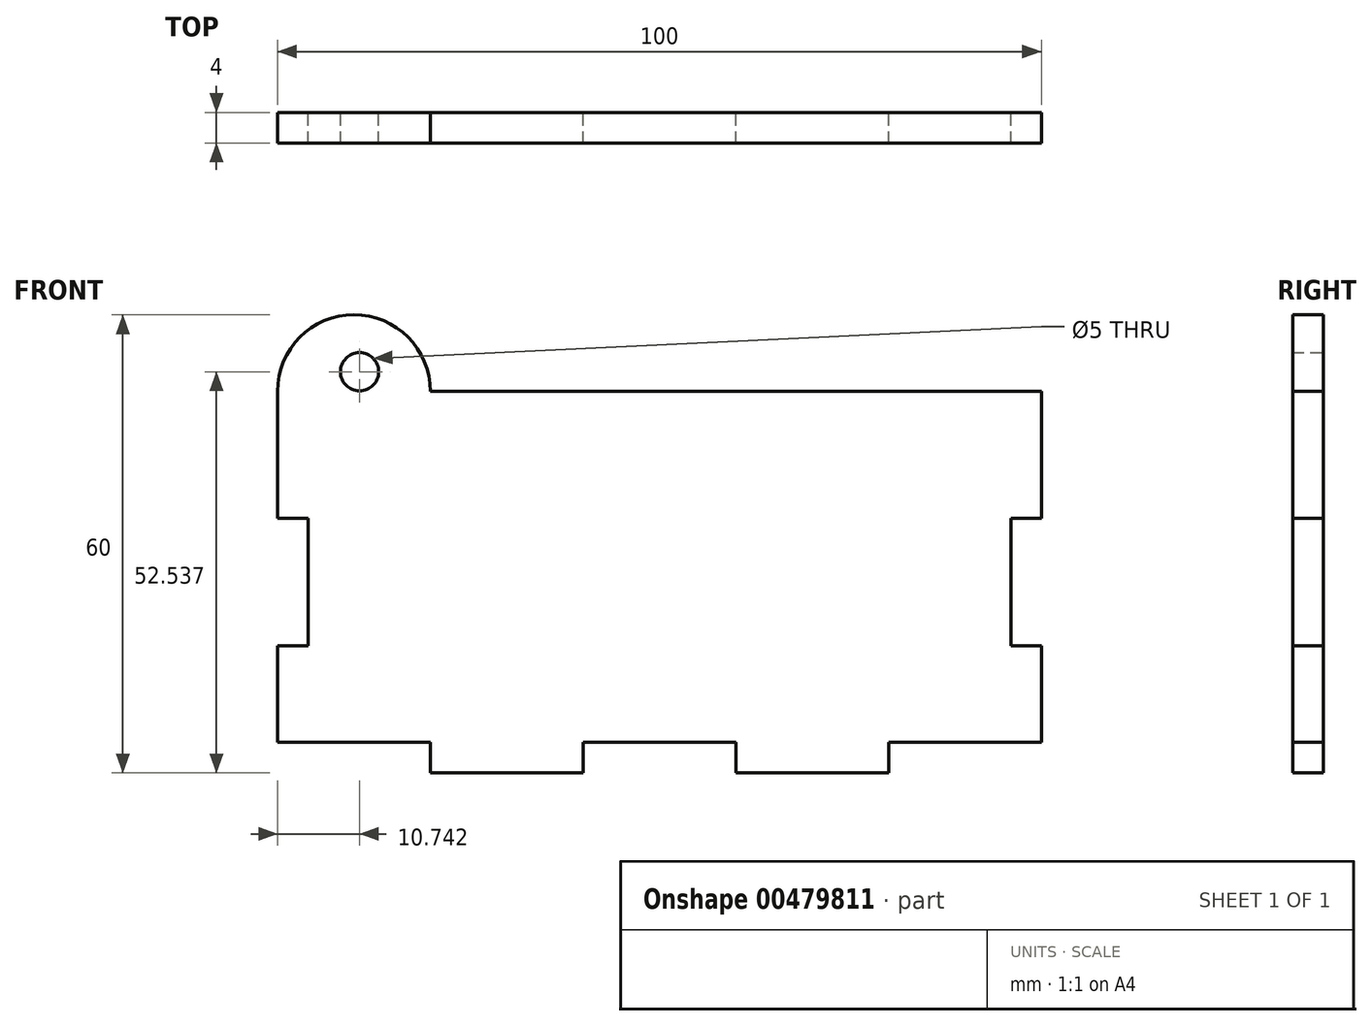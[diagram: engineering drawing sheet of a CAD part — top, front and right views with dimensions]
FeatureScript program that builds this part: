
annotation { "Feature Type Name" : "Feature", "Feature Type Description" : "" }
export const myFeature = defineFeature(function(context is Context, id is Id, definition is map)
    precondition{}
    {
        {
            var Q0;
            Q0=qCreatedBy(makeId("Front.planeOp"),FACE);
            var sketch = newSketch(context, id + "F0", { "sketchPlane" : qUnion([Q0])});
            skLineSegment(sketch, "E0.bottom", {"start": v(0, 0) * mm, "end": v(100, 0) * mm});
            skLineSegment(sketch, "E0.top", {"start": v(0, 50) * mm, "end": v(100, 50) * mm});
            skLineSegment(sketch, "E0.left", {"start": v(0, 0) * mm, "end": v(0, 50) * mm});
            skLineSegment(sketch, "E0.right", {"start": v(100, 0) * mm, "end": v(100, 50) * mm});
            skSolve(sketch);
        }
        {
            var Q0;
            Q0 = qSketchRegion(id + "F0", true);
            extrude(context, id + "F1", {"entities" : qUnion([Q0]), "depth" : 4 * mm});
        }
        {
            var Q0;
            Q0=qCreatedBy(makeId("Front.planeOp"),FACE);
            var sketch = newSketch(context, id + "F2", { "sketchPlane" : qUnion([Q0])});
            skLineSegment(sketch, "E1.bottom", {"start": v(0, 16.67) * mm, "end": v(4, 16.67) * mm});
            skLineSegment(sketch, "E1.top", {"start": v(0, 33.33) * mm, "end": v(4, 33.33) * mm});
            skLineSegment(sketch, "E1.left", {"start": v(0, 16.67) * mm, "end": v(0, 33.33) * mm});
            skLineSegment(sketch, "E1.right", {"start": v(4, 16.67) * mm, "end": v(4, 33.33) * mm});
            skLineSegment(sketch, "E2.bottom", {"start": v(0, 0) * mm, "end": v(20, 0) * mm});
            skLineSegment(sketch, "E2.top", {"start": v(0, 4) * mm, "end": v(20, 4) * mm});
            skLineSegment(sketch, "E2.left", {"start": v(0, 0) * mm, "end": v(0, 4) * mm});
            skLineSegment(sketch, "E2.right", {"start": v(20, 0) * mm, "end": v(20, 4) * mm});
            skLineSegment(sketch, "E3.bottom", {"start": v(40, 0) * mm, "end": v(60, 0) * mm});
            skLineSegment(sketch, "E3.top", {"start": v(40, 4) * mm, "end": v(60, 4) * mm});
            skLineSegment(sketch, "E3.left", {"start": v(40, 0) * mm, "end": v(40, 4) * mm});
            skLineSegment(sketch, "E3.right", {"start": v(60, 0) * mm, "end": v(60, 4) * mm});
            skLineSegment(sketch, "E4.bottom", {"start": v(80, 0) * mm, "end": v(100, 0) * mm});
            skLineSegment(sketch, "E4.top", {"start": v(80, 4) * mm, "end": v(100, 4) * mm});
            skLineSegment(sketch, "E4.left", {"start": v(80, 0) * mm, "end": v(80, 4) * mm});
            skLineSegment(sketch, "E4.right", {"start": v(100, 0) * mm, "end": v(100, 4) * mm});
            skLineSegment(sketch, "E5.bottom", {"start": v(100, 16.67) * mm, "end": v(96, 16.67) * mm});
            skLineSegment(sketch, "E5.top", {"start": v(100, 33.33) * mm, "end": v(96, 33.33) * mm});
            skLineSegment(sketch, "E5.left", {"start": v(100, 16.67) * mm, "end": v(100, 33.33) * mm});
            skLineSegment(sketch, "E5.right", {"start": v(96, 16.67) * mm, "end": v(96, 33.33) * mm});
            skSolve(sketch);
        }
        {
            var Q0;
            Q0 = qSketchRegion(id + "F2", true);
            extrude(context, id + "F3", {"entities" : qUnion([Q0]), "operationType" : NewBodyOperationType.REMOVE, "depth" : 4 * mm});
        }
        {
            var Q0;
            Q0=qCreatedBy(makeId("Front.planeOp"),FACE);
            var sketch = newSketch(context, id + "F4", { "sketchPlane" : qUnion([Q0])});
            skCircle(sketch, "E6", {"center": v(10, 50) * mm, "radius": 10 * mm});
            skSolve(sketch);
        }
        {
            var Q0;
            Q0 = qSketchRegion(id + "F4", true);
            extrude(context, id + "F5", {"entities" : qUnion([Q0]), "operationType" : NewBodyOperationType.ADD, "depth" : 4 * mm});
        }
        {
            var Q0;
            Q0=qCreatedBy(makeId("Front.planeOp"),FACE);
            var sketch = newSketch(context, id + "F6", { "sketchPlane" : qUnion([Q0])});
            skCircle(sketch, "E7", {"center": v(10.74, 52.54) * mm, "radius": 2.5 * mm});
            skSolve(sketch);
        }
        {
            var Q0;
            Q0 = qSketchRegion(id + "F6", true);
            extrude(context, id + "F7", {"entities" : qUnion([Q0]), "operationType" : NewBodyOperationType.REMOVE, "depth" : 4 * mm});
        }
    });
